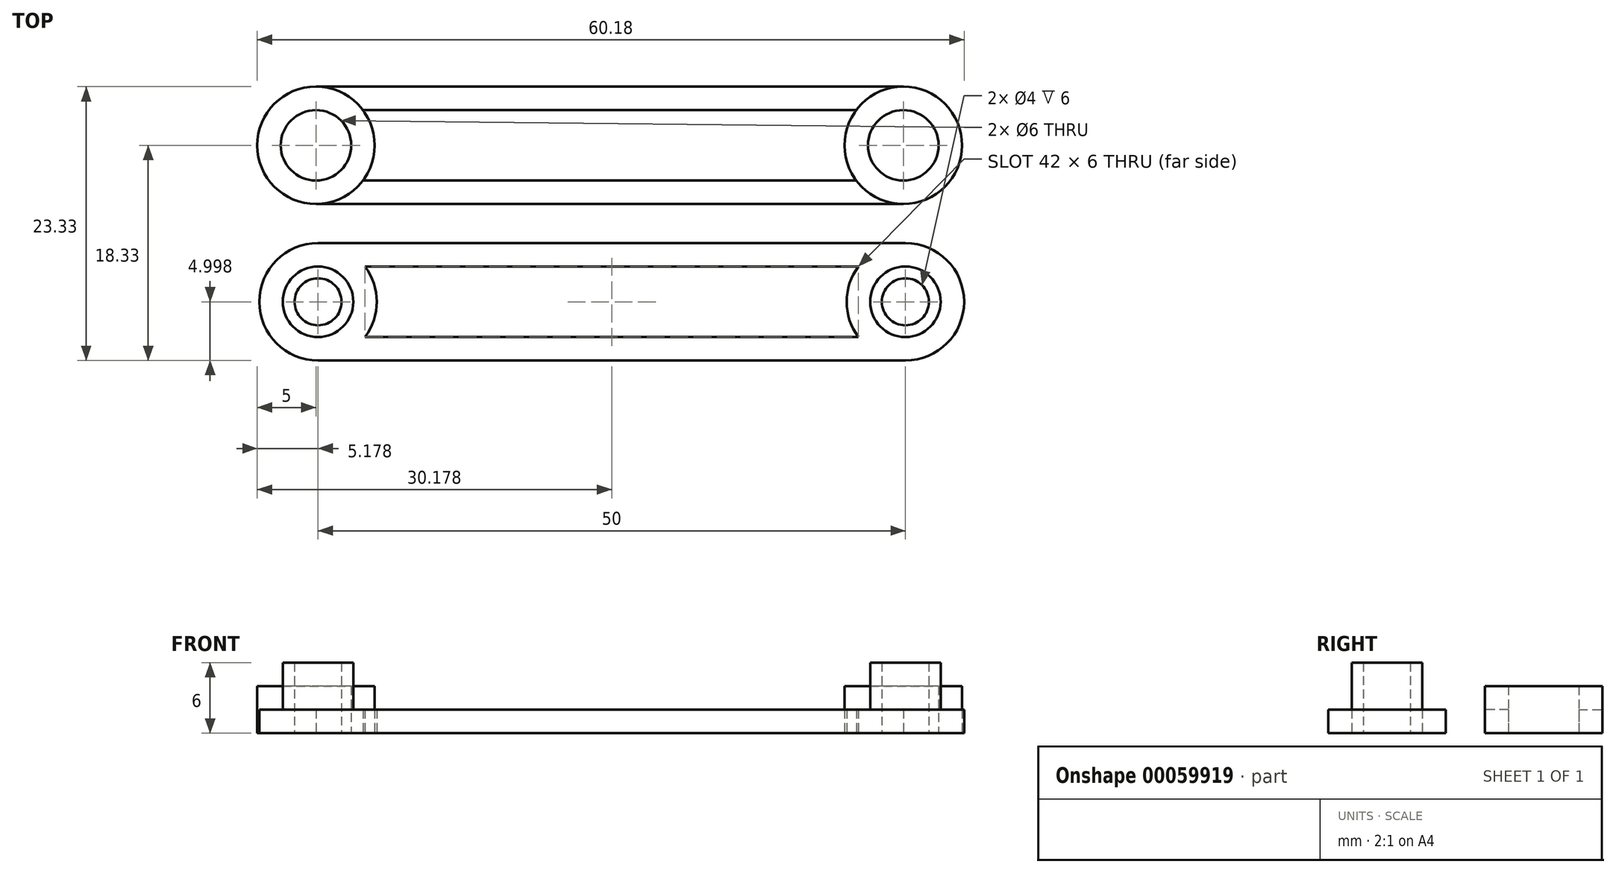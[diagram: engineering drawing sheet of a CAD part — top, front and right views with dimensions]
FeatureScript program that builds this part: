
annotation { "Feature Type Name" : "Feature", "Feature Type Description" : "" }
export const myFeature = defineFeature(function(context is Context, id is Id, definition is map)
    precondition{}
    {
        {
            var Q0;
            Q0=qCreatedBy(makeId("Top.planeOp"),FACE);
            var sketch = newSketch(context, id + "F0", { "sketchPlane" : qUnion([Q0])});
            skCircle(sketch, "E0", {"center": v(25, 0) * mm, "radius": 5 * mm});
            skCircle(sketch, "E1.0", {"center": v(25, 0) * mm, "radius": 3 * mm});
            skCircle(sketch, "E2", {"center": v(-25, 0) * mm, "radius": 5 * mm});
            skCircle(sketch, "E3.0", {"center": v(-25, 0) * mm, "radius": 3 * mm});
            skLineSegment(sketch, "E4.0", {"start": v(-25, -5) * mm, "end": v(25, -5) * mm});
            skLineSegment(sketch, "E5.0", {"start": v(-25, 5) * mm, "end": v(25, 5) * mm});
            skLineSegment(sketch, "E6.0", {"start": v(-21, -3) * mm, "end": v(21, -3) * mm});
            skLineSegment(sketch, "E7.0", {"start": v(-21, 3) * mm, "end": v(21, 3) * mm});
            skSolve(sketch);
        }
        {
            var Q0;
            Q0=makeQuery(id+"F0.imprint","IMPRINT",FACE,{"disambiguationData":[TD([[makeQuery(id+"F0.imprint","IMPRINT",EDGE,{"derivedFrom":sQuery(id+"F0.wireOp",EDGE,"E1.0")}),-1.0]])]});
            var Q1;
            Q1=makeQuery(id+"F0.imprint","IMPRINT",FACE,{"disambiguationData":[TD([[makeQuery(id+"F0.imprint","IMPRINT",EDGE,{"derivedFrom":sQuery(id+"F0.wireOp",EDGE,"E3.0")}),-1.0]])]});
            extrude(context, id + "F1", {"entities" : qUnion([Q0, Q1]), "depth" : 4 * mm});
        }
        {
            var Q0;
            {var subQ0=sQuery(id+"F0.wireOp",EDGE,"E5.0");Q0=makeQuery(id+"F0.imprint","IMPRINT",FACE,{"disambiguationData":[TD([[makeQuery(id+"F0.imprint","IMPRINT",EDGE,{"derivedFrom":subQ0}),-1.0]])]});}
            var Q1;
            {var subQ0=sQuery(id+"F0.wireOp",EDGE,"E4.0");Q1=makeQuery(id+"F0.imprint","IMPRINT",FACE,{"disambiguationData":[TD([[makeQuery(id+"F0.imprint","IMPRINT",EDGE,{"derivedFrom":subQ0}),1.0]])]});}
            extrude(context, id + "F2", {"entities" : qUnion([Q0, Q1]), "depth" : 2 * mm});
        }
        {
            var Q0;
            Q0=qCreatedBy(makeId("Top.planeOp"),FACE);
            var sketch = newSketch(context, id + "F3", { "sketchPlane" : qUnion([Q0])});
            skCircle(sketch, "E8", {"center": v(25.18, -13.33) * mm, "radius": 5 * mm});
            skCircle(sketch, "E9.0", {"center": v(25.18, -13.33) * mm, "radius": 3 * mm});
            skCircle(sketch, "E10", {"center": v(-24.82, -13.33) * mm, "radius": 5 * mm});
            skCircle(sketch, "E11.0", {"center": v(-24.82, -13.33) * mm, "radius": 3 * mm});
            skLineSegment(sketch, "E12.0", {"start": v(-24.82, -18.33) * mm, "end": v(25.18, -18.33) * mm});
            skLineSegment(sketch, "E13.0", {"start": v(-24.82, -8.33) * mm, "end": v(25.18, -8.33) * mm});
            skLineSegment(sketch, "E14.0", {"start": v(-20.82, -16.33) * mm, "end": v(21.18, -16.33) * mm});
            skLineSegment(sketch, "E15.0", {"start": v(-20.82, -10.33) * mm, "end": v(21.18, -10.33) * mm});
            skCircle(sketch, "E16.0", {"center": v(25.18, -13.33) * mm, "radius": 2 * mm});
            skCircle(sketch, "E17.0", {"center": v(-24.82, -13.33) * mm, "radius": 2 * mm});
            skSolve(sketch);
        }
        {
            var Q0;
            Q0 = qSketchRegion(id + "F3", true);
            extrude(context, id + "F4", {"entities" : qUnion([Q0]), "depth" : 2 * mm});
        }
        {
            var Q0;
            Q0=makeQuery(id+"F3.imprint","IMPRINT",FACE,{"disambiguationData":[TD([[makeQuery(id+"F3.imprint","IMPRINT",EDGE,{"derivedFrom":sQuery(id+"F3.wireOp",EDGE,"E11.0")}),1.0]])]});
            var Q1;
            Q1=makeQuery(id+"F3.imprint","IMPRINT",FACE,{"disambiguationData":[TD([[makeQuery(id+"F3.imprint","IMPRINT",EDGE,{"derivedFrom":sQuery(id+"F3.wireOp",EDGE,"E9.0")}),1.0]])]});
            extrude(context, id + "F5", {"entities" : qUnion([Q0, Q1]), "operationType" : NewBodyOperationType.ADD, "depth" : 6 * mm});
        }
    });
